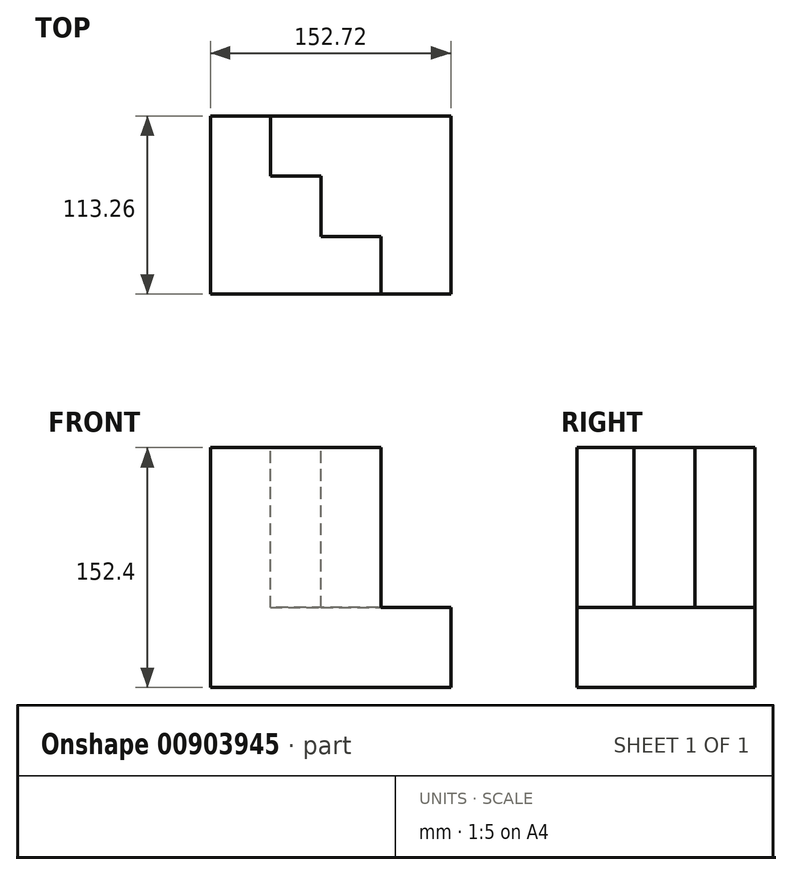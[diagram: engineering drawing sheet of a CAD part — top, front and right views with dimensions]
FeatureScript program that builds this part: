
annotation { "Feature Type Name" : "Feature", "Feature Type Description" : "" }
export const myFeature = defineFeature(function(context is Context, id is Id, definition is map)
    precondition{}
    {
        {
            var Q0;
            Q0=qCreatedBy(makeId("Top.planeOp"),FACE);
            var sketch = newSketch(context, id + "F0", { "sketchPlane" : qUnion([Q0])});
            skLineSegment(sketch, "E0.bottom", {"start": v(76.36, 56.63) * mm, "end": v(-76.36, 56.63) * mm});
            skLineSegment(sketch, "E0.top", {"start": v(76.36, -56.63) * mm, "end": v(-76.36, -56.63) * mm});
            skLineSegment(sketch, "E0.left", {"start": v(76.36, 56.63) * mm, "end": v(76.36, -56.63) * mm});
            skLineSegment(sketch, "E0.right", {"start": v(-76.36, 56.63) * mm, "end": v(-76.36, -56.63) * mm});
            skPoint(sketch, "E0.middle", {"position": v(0, 0) * mm});
            skSolve(sketch);
        }
        {
            var Q0;
            Q0=makeQuery(id+"F0.imprint","IMPRINT",FACE,{"disambiguationData":[TD([[makeQuery(id+"F0.imprint","IMPRINT",EDGE,{"derivedFrom":sQuery(id+"F0.wireOp",EDGE,"E0.bottom")}),1.0]])]});
            extrude(context, id + "F1", {"entities" : qUnion([Q0]), "depth" : 152.4 * mm, "offsetDistance" : 25.4 * mm});
        }
        {
            var Q0;
            Q0=makeQuery(id+"F1.opExtrude","CAP_FACE",FACE,{"disambiguationData":[OSD([sQuery(id+"F0.wireOp",EDGE,"E0.bottom"),sQuery(id+"F0.wireOp",EDGE,"E0.top"),sQuery(id+"F0.wireOp",EDGE,"E0.left"),sQuery(id+"F0.wireOp",EDGE,"E0.right")])],"isStart":false});
            var sketch = newSketch(context, id + "F2", { "sketchPlane" : qUnion([Q0])});
            skLineSegment(sketch, "E1", {"start": v(-76.36, 56.63) * mm, "end": v(-38.26, 56.63) * mm});
            skLineSegment(sketch, "E2", {"start": v(-38.26, 56.63) * mm, "end": v(-38.26, 18.53) * mm});
            skLineSegment(sketch, "E3", {"start": v(-38.26, 18.53) * mm, "end": v(-6, 18.53) * mm});
            skLineSegment(sketch, "E4", {"start": v(-6, 18.53) * mm, "end": v(-6, -20.16) * mm});
            skLineSegment(sketch, "E5", {"start": v(-6, -20.16) * mm, "end": v(32.1, -20.16) * mm});
            skLineSegment(sketch, "E6", {"start": v(32.1, -20.16) * mm, "end": v(32.1, -56.63) * mm});
            skSolve(sketch);
        }
        {
            var Q0;
            {var subQ0=sQuery(id+"F2.wireOp",EDGE,"E2");Q0=makeQuery(id+"F2.imprint","IMPRINT",FACE,{"disambiguationData":[TD([[makeQuery(id+"F2.imprint","IMPRINT",EDGE,{"derivedFrom":subQ0}),1.0]])]});}
            extrude(context, id + "F3", {"entities" : qUnion([Q0]), "operationType" : NewBodyOperationType.REMOVE, "oppositeDirection" : true, "depth" : 101.6 * mm, "offsetDistance" : 25.4 * mm});
        }
    });
